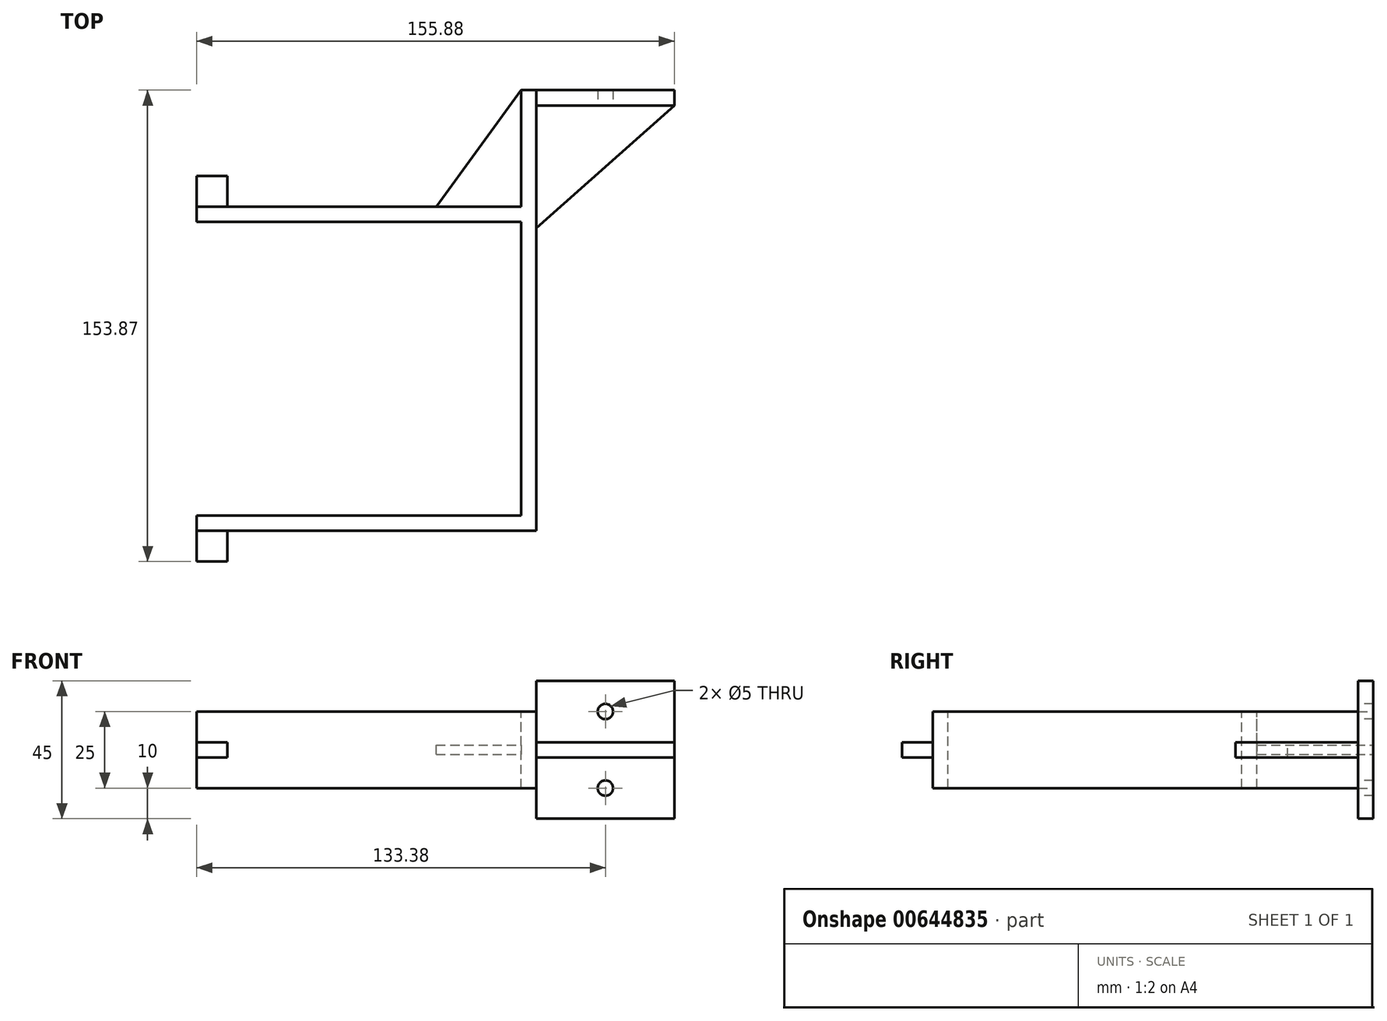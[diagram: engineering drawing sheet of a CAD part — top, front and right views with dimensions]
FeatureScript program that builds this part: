
annotation { "Feature Type Name" : "Feature", "Feature Type Description" : "" }
export const myFeature = defineFeature(function(context is Context, id is Id, definition is map)
    precondition{}
    {
        {
            var Q0;
            Q0=qCreatedBy(makeId("Top.planeOp"),FACE);
            var sketch = newSketch(context, id + "F0", { "sketchPlane" : qUnion([Q0])});
            skLineSegment(sketch, "E0", {"start": v(0, 0) * mm, "end": v(0, 0) * mm});
            skLineSegment(sketch, "E1", {"start": v(0, 0) * mm, "end": v(-10, 0) * mm});
            skLineSegment(sketch, "E2", {"start": v(-10, 0) * mm, "end": v(-10, -5) * mm});
            skLineSegment(sketch, "E3", {"start": v(-10, -5) * mm, "end": v(100.88, -5) * mm});
            skLineSegment(sketch, "E4", {"start": v(100.88, -5) * mm, "end": v(100.88, 133.87) * mm});
            skLineSegment(sketch, "E5", {"start": v(100.88, 133.87) * mm, "end": v(145.88, 133.87) * mm});
            skLineSegment(sketch, "E6", {"start": v(145.88, 133.87) * mm, "end": v(145.88, 138.87) * mm});
            skLineSegment(sketch, "E7", {"start": v(145.88, 138.87) * mm, "end": v(95.88, 138.87) * mm});
            skLineSegment(sketch, "E8", {"start": v(95.88, 138.87) * mm, "end": v(95.88, 100.88) * mm});
            skLineSegment(sketch, "E9", {"start": v(95.88, 100.88) * mm, "end": v(-10, 100.88) * mm});
            skLineSegment(sketch, "E10", {"start": v(-10, 100.88) * mm, "end": v(-10, 95.88) * mm});
            skLineSegment(sketch, "E11", {"start": v(-10, 95.88) * mm, "end": v(0, 95.88) * mm});
            skLineSegment(sketch, "E12", {"start": v(0, 95.88) * mm, "end": v(0, 95.88) * mm});
            skLineSegment(sketch, "E13", {"start": v(0, 95.88) * mm, "end": v(95.88, 95.88) * mm});
            skLineSegment(sketch, "E14", {"start": v(95.88, 95.88) * mm, "end": v(95.88, 0) * mm});
            skLineSegment(sketch, "E15", {"start": v(95.88, 0) * mm, "end": v(0, 0) * mm});
            skSolve(sketch);
        }
        {
            var Q0;
            Q0=qSketchRegion(id+"F0",true);
            extrude(context, id + "F1", {"entities" : qUnion([Q0]), "oppositeDirection" : true, "depth" : 25 * mm, "offsetDistance" : 25 * mm});
        }
        {
            var Q0;
            Q0=makeQuery(id+"F1.opExtrude","SWEPT_FACE",FACE,{"disambiguationData":[OSD([sQuery(id+"F0.wireOp",EDGE,"E7")])]});
            var sketch = newSketch(context, id + "F2", { "sketchPlane" : qUnion([Q0])});
            skLineSegment(sketch, "E16.bottom", {"start": v(-95.88, -17) * mm, "end": v(-56.33, -17) * mm});
            skLineSegment(sketch, "E16.top", {"start": v(-95.88, -8) * mm, "end": v(-56.33, -8) * mm});
            skLineSegment(sketch, "E16.left", {"start": v(-95.88, -17) * mm, "end": v(-95.88, -8) * mm});
            skLineSegment(sketch, "E16.right", {"start": v(-56.33, -17) * mm, "end": v(-56.33, -8) * mm});
            skSolve(sketch);
        }
        {
            var Q0;
            Q0=makeQuery(id+"F2.imprint","IMPRINT",FACE,{"disambiguationData":[TD([[makeQuery(id+"F2.imprint","IMPRINT",EDGE,{"derivedFrom":sQuery(id+"F2.wireOp",EDGE,"E16.bottom")}),1.0]])]});
            extrude(context, id + "F3", {"entities" : qUnion([Q0]), "operationType" : NewBodyOperationType.REMOVE, "oppositeDirection" : true, "depth" : 33 * mm, "offsetDistance" : 25 * mm});
        }
        {
            var Q0;
            Q0=makeQuery(id+"F1.opExtrude","SWEPT_FACE",FACE,{"disambiguationData":[OSD([sQuery(id+"F0.wireOp",EDGE,"E3")])]});
            var sketch = newSketch(context, id + "F4", { "sketchPlane" : qUnion([Q0])});
            skLineSegment(sketch, "E17.bottom", {"start": v(-10, -15) * mm, "end": v(0, -15) * mm});
            skLineSegment(sketch, "E17.top", {"start": v(-10, -10) * mm, "end": v(0, -10) * mm});
            skLineSegment(sketch, "E17.left", {"start": v(-10, -15) * mm, "end": v(-10, -10) * mm});
            skLineSegment(sketch, "E17.right", {"start": v(0, -15) * mm, "end": v(0, -10) * mm});
            skSolve(sketch);
        }
        {
            var Q0;
            Q0=makeQuery(id+"F4.imprint","IMPRINT",FACE,{"disambiguationData":[TD([[makeQuery(id+"F4.imprint","IMPRINT",EDGE,{"derivedFrom":sQuery(id+"F4.wireOp",EDGE,"E17.bottom")}),1.0]])]});
            extrude(context, id + "F5", {"entities" : qUnion([Q0]), "operationType" : NewBodyOperationType.ADD, "depth" : 10 * mm, "offsetDistance" : 25 * mm});
        }
        {
            var Q0;
            Q0=makeQuery(id+"F3.boolean.opBoolean","MERGE",FACE,{"derivedFrom":[makeQuery(id+"F1.opExtrude","SWEPT_FACE",FACE,{"disambiguationData":[OSD([sQuery(id+"F0.wireOp",EDGE,"E9")])]}),makeQuery(id+"F3.opExtrude","CAP_FACE",FACE,{"disambiguationData":[OSD([sQuery(id+"F2.wireOp",EDGE,"E16.bottom"),sQuery(id+"F2.wireOp",EDGE,"E16.top"),sQuery(id+"F2.wireOp",EDGE,"E16.left"),sQuery(id+"F2.wireOp",EDGE,"E16.right")])],"isStart":false})]});
            var sketch = newSketch(context, id + "F6", { "sketchPlane" : qUnion([Q0])});
            skLineSegment(sketch, "E18.bottom", {"start": v(10, -10) * mm, "end": v(0, -10) * mm});
            skLineSegment(sketch, "E18.top", {"start": v(10, -15) * mm, "end": v(0, -15) * mm});
            skLineSegment(sketch, "E18.left", {"start": v(10, -10) * mm, "end": v(10, -15) * mm});
            skLineSegment(sketch, "E18.right", {"start": v(0, -10) * mm, "end": v(0, -15) * mm});
            skSolve(sketch);
        }
        {
            var Q0;
            Q0=makeQuery(id+"F6.imprint","IMPRINT",FACE,{"disambiguationData":[TD([[makeQuery(id+"F6.imprint","IMPRINT",EDGE,{"derivedFrom":sQuery(id+"F6.wireOp",EDGE,"E18.bottom")}),1.0]])]});
            extrude(context, id + "F7", {"entities" : qUnion([Q0]), "operationType" : NewBodyOperationType.ADD, "depth" : 10 * mm, "offsetDistance" : 25 * mm});
        }
        {
            var Q0;
            Q0=makeQuery(id+"F1.opExtrude","SWEPT_FACE",FACE,{"disambiguationData":[OSD([sQuery(id+"F0.wireOp",EDGE,"E5")])]});
            var sketch = newSketch(context, id + "F8", { "sketchPlane" : qUnion([Q0])});
            skLineSegment(sketch, "E19.bottom", {"start": v(100.88, -10) * mm, "end": v(145.88, -10) * mm});
            skLineSegment(sketch, "E19.top", {"start": v(100.88, -15) * mm, "end": v(145.88, -15) * mm});
            skLineSegment(sketch, "E19.left", {"start": v(100.88, -10) * mm, "end": v(100.88, -15) * mm});
            skLineSegment(sketch, "E19.right", {"start": v(145.88, -10) * mm, "end": v(145.88, -15) * mm});
            skSolve(sketch);
        }
        {
            var Q0;
            Q0=makeQuery(id+"F8.imprint","IMPRINT",FACE,{"disambiguationData":[TD([[makeQuery(id+"F8.imprint","IMPRINT",EDGE,{"derivedFrom":sQuery(id+"F8.wireOp",EDGE,"E19.bottom")}),-1.0]])]});
            extrude(context, id + "F9", {"entities" : qUnion([Q0]), "operationType" : NewBodyOperationType.ADD, "depth" : 40 * mm, "offsetDistance" : 25 * mm});
        }
        {
            var Q0;
            Q0=makeQuery(id+"F9.opExtrude","SWEPT_FACE",FACE,{"disambiguationData":[OSD([sQuery(id+"F8.wireOp",EDGE,"E19.top")])]});
            var sketch = newSketch(context, id + "F10", { "sketchPlane" : qUnion([Q0])});
            skLineSegment(sketch, "E20", {"start": v(100.88, -93.87) * mm, "end": v(145.88, -133.87) * mm});
            skLineSegment(sketch, "E21", {"start": v(100.88, -93.87) * mm, "end": v(145.88, -93.87) * mm});
            skLineSegment(sketch, "E22", {"start": v(145.88, -93.87) * mm, "end": v(145.88, -133.87) * mm});
            skLineSegment(sketch, "E23", {"start": v(145.88, -67.74) * mm, "end": v(136.05, -67.74) * mm});
            skSolve(sketch);
        }
        {
            var Q0;
            Q0=makeQuery(id+"F10.imprint","IMPRINT",FACE,{"disambiguationData":[TD([[makeQuery(id+"F10.imprint","IMPRINT",EDGE,{"derivedFrom":sQuery(id+"F10.wireOp",EDGE,"E20")}),1.0]])]});
            extrude(context, id + "F11", {"entities" : qUnion([Q0]), "operationType" : NewBodyOperationType.REMOVE, "endBound" : BoundingType.UP_TO_NEXT, "oppositeDirection" : true, "depth" : 25 * mm, "offsetDistance" : 25 * mm});
        }
        {
            var Q0;
            {var subQ0=sQuery(id+"F0.wireOp",EDGE,"E9");var subQ1=sQuery(id+"F0.wireOp",EDGE,"E8");Q0=makeQuery(id+"F3OWXgqpNNXNJOV_1.boolean.opBoolean","MERGE",FACE,{"derivedFrom":[makeQuery(id+"F1.opExtrude","CAP_FACE",FACE,{"disambiguationData":[OSD([sQuery(id+"F0.wireOp",EDGE,"E1"),sQuery(id+"F0.wireOp",EDGE,"E2"),sQuery(id+"F0.wireOp",EDGE,"E3"),sQuery(id+"F0.wireOp",EDGE,"E4"),sQuery(id+"F0.wireOp",EDGE,"E5"),sQuery(id+"F0.wireOp",EDGE,"E6"),sQuery(id+"F0.wireOp",EDGE,"E7"),subQ1,subQ0,sQuery(id+"F0.wireOp",EDGE,"E10"),sQuery(id+"F0.wireOp",EDGE,"E11"),sQuery(id+"F0.wireOp",EDGE,"E13"),sQuery(id+"F0.wireOp",EDGE,"E14"),sQuery(id+"F0.wireOp",EDGE,"E15")])],"isStart":false}),makeQuery(id+"F3OWXgqpNNXNJOV_1.opExtrude","CAP_FACE",FACE,{"disambiguationData":[OSD([subQ1,subQ0,sQuery(id+"FQ3WUeavLo7wkBa_1.wireOp",EDGE,"9ih6puce-coCi-Da0f-sg7k-QBfH5EJdpGK5")])],"isStart":false})]});}
            var sketch = newSketch(context, id + "F12", { "sketchPlane" : qUnion([Q0])});
            skLineSegment(sketch, "E24.bottom", {"start": v(100.88, -133.87) * mm, "end": v(145.88, -133.87) * mm});
            skLineSegment(sketch, "E24.top", {"start": v(100.88, -138.87) * mm, "end": v(145.88, -138.87) * mm});
            skLineSegment(sketch, "E24.left", {"start": v(100.88, -133.87) * mm, "end": v(100.88, -138.87) * mm});
            skLineSegment(sketch, "E24.right", {"start": v(145.88, -133.87) * mm, "end": v(145.88, -138.87) * mm});
            skSolve(sketch);
        }
        {
            var Q0;
            Q0=makeQuery(id+"F12.imprint","IMPRINT",FACE,{"disambiguationData":[TD([[makeQuery(id+"F12.imprint","IMPRINT",EDGE,{"derivedFrom":sQuery(id+"F12.wireOp",EDGE,"E24.bottom")}),-1.0]])]});
            extrude(context, id + "F13", {"entities" : qUnion([Q0]), "operationType" : NewBodyOperationType.ADD, "depth" : 10 * mm, "offsetDistance" : 25 * mm});
        }
        {
            var Q0;
            {var subQ0=sQuery(id+"F0.wireOp",EDGE,"E9");var subQ1=sQuery(id+"F0.wireOp",EDGE,"E8");Q0=makeQuery(id+"F3OWXgqpNNXNJOV_1.boolean.opBoolean","MERGE",FACE,{"derivedFrom":[makeQuery(id+"F1.opExtrude","CAP_FACE",FACE,{"disambiguationData":[OSD([sQuery(id+"F0.wireOp",EDGE,"E1"),sQuery(id+"F0.wireOp",EDGE,"E2"),sQuery(id+"F0.wireOp",EDGE,"E3"),sQuery(id+"F0.wireOp",EDGE,"E4"),sQuery(id+"F0.wireOp",EDGE,"E5"),sQuery(id+"F0.wireOp",EDGE,"E6"),sQuery(id+"F0.wireOp",EDGE,"E7"),subQ1,subQ0,sQuery(id+"F0.wireOp",EDGE,"E10"),sQuery(id+"F0.wireOp",EDGE,"E11"),sQuery(id+"F0.wireOp",EDGE,"E13"),sQuery(id+"F0.wireOp",EDGE,"E14"),sQuery(id+"F0.wireOp",EDGE,"E15")])],"isStart":true}),makeQuery(id+"F3OWXgqpNNXNJOV_1.opExtrude","CAP_FACE",FACE,{"disambiguationData":[OSD([subQ1,subQ0,sQuery(id+"FQ3WUeavLo7wkBa_1.wireOp",EDGE,"9ih6puce-coCi-Da0f-sg7k-QBfH5EJdpGK5")])],"isStart":true})]});}
            var sketch = newSketch(context, id + "F14", { "sketchPlane" : qUnion([Q0])});
            skLineSegment(sketch, "E25.bottom", {"start": v(100.88, 133.87) * mm, "end": v(145.88, 133.87) * mm});
            skLineSegment(sketch, "E25.top", {"start": v(100.88, 138.87) * mm, "end": v(145.88, 138.87) * mm});
            skLineSegment(sketch, "E25.left", {"start": v(100.88, 133.87) * mm, "end": v(100.88, 138.87) * mm});
            skLineSegment(sketch, "E25.right", {"start": v(145.88, 133.87) * mm, "end": v(145.88, 138.87) * mm});
            skSolve(sketch);
        }
        {
            var Q0;
            Q0=makeQuery(id+"F14.imprint","IMPRINT",FACE,{"disambiguationData":[TD([[makeQuery(id+"F14.imprint","IMPRINT",EDGE,{"derivedFrom":sQuery(id+"F14.wireOp",EDGE,"E25.bottom")}),1.0]])]});
            extrude(context, id + "F15", {"entities" : qUnion([Q0]), "operationType" : NewBodyOperationType.ADD, "depth" : 10 * mm, "offsetDistance" : 25 * mm});
        }
        {
            var Q0;
            Q0=makeQuery(id+"F1.opExtrude","SWEPT_FACE",FACE,{"disambiguationData":[OSD([sQuery(id+"F0.wireOp",EDGE,"E8")])]});
            var sketch = newSketch(context, id + "F16", { "sketchPlane" : qUnion([Q0])});
            skLineSegment(sketch, "E26.bottom", {"start": v(-100.88, -11) * mm, "end": v(-138.87, -11) * mm});
            skLineSegment(sketch, "E26.top", {"start": v(-100.88, -14) * mm, "end": v(-138.87, -14) * mm});
            skLineSegment(sketch, "E26.left", {"start": v(-100.88, -11) * mm, "end": v(-100.88, -14) * mm});
            skLineSegment(sketch, "E26.right", {"start": v(-138.87, -11) * mm, "end": v(-138.87, -14) * mm});
            skSolve(sketch);
        }
        {
            var Q0;
            Q0=makeQuery(id+"F16.imprint","IMPRINT",FACE,{"disambiguationData":[TD([[makeQuery(id+"F16.imprint","IMPRINT",EDGE,{"derivedFrom":sQuery(id+"F16.wireOp",EDGE,"E26.bottom")}),1.0]])]});
            extrude(context, id + "F17", {"entities" : qUnion([Q0]), "operationType" : NewBodyOperationType.ADD, "depth" : 27.7 * mm, "offsetDistance" : 25 * mm});
        }
        {
            var Q0;
            Q0=makeQuery(id+"F17.opExtrude","SWEPT_FACE",FACE,{"disambiguationData":[OSD([sQuery(id+"F16.wireOp",EDGE,"E26.top")])]});
            var sketch = newSketch(context, id + "F18", { "sketchPlane" : qUnion([Q0])});
            skLineSegment(sketch, "E27", {"start": v(95.88, -138.87) * mm, "end": v(68.18, -100.88) * mm});
            skLineSegment(sketch, "E28", {"start": v(68.18, -100.88) * mm, "end": v(68.18, -138.87) * mm});
            skLineSegment(sketch, "E29", {"start": v(68.18, -138.87) * mm, "end": v(95.88, -138.87) * mm});
            skSolve(sketch);
        }
        {
            var Q0;
            Q0=makeQuery(id+"F18.imprint","IMPRINT",FACE,{"disambiguationData":[TD([[makeQuery(id+"F18.imprint","IMPRINT",EDGE,{"derivedFrom":sQuery(id+"F18.wireOp",EDGE,"E27")}),1.0]])]});
            extrude(context, id + "F19", {"entities" : qUnion([Q0]), "operationType" : NewBodyOperationType.REMOVE, "oppositeDirection" : true, "depth" : 25 * mm, "offsetDistance" : 25 * mm});
        }
        {
            var Q0;
            {var subQ2=sQuery(id+"F0.wireOp",EDGE,"E5");Q0=makeQuery(id+"F15.boolean.opBoolean","MERGE",FACE,{"derivedFrom":[makeQuery(id+"F9.boolean.opBoolean","SPLIT",FACE,{"disambiguationData":[TD([makeQuery(id+"F9.opExtrude","SWEPT_FACE",FACE,{"disambiguationData":[OSD([sQuery(id+"F8.wireOp",EDGE,"E19.bottom")])]})])],"derivedFrom":makeQuery(id+"F1.opExtrude","SWEPT_FACE",FACE,{"disambiguationData":[OSD([subQ2])]})}),makeQuery(id+"F15.opExtrude","SWEPT_FACE",FACE,{"disambiguationData":[OSD([sQuery(id+"F14.wireOp",EDGE,"E25.bottom")])]})]});}
            var sketch = newSketch(context, id + "F20", { "sketchPlane" : qUnion([Q0])});
            skCircle(sketch, "E30", {"center": v(123.38, 0) * mm, "radius": 2.5 * mm});
            skCircle(sketch, "E31", {"center": v(123.38, -25) * mm, "radius": 2.5 * mm});
            skSolve(sketch);
        }
        {
            var Q0;
            Q0=makeQuery(id+"F20.imprint","IMPRINT",FACE,{"disambiguationData":[TD([[makeQuery(id+"F20.imprint","IMPRINT",EDGE,{"derivedFrom":sQuery(id+"F20.wireOp",EDGE,"E30")}),1.0]])]});
            var Q1;
            Q1=makeQuery(id+"F20.imprint","IMPRINT",FACE,{"disambiguationData":[TD([[makeQuery(id+"F20.imprint","IMPRINT",EDGE,{"derivedFrom":sQuery(id+"F20.wireOp",EDGE,"E31")}),1.0]])]});
            extrude(context, id + "F21", {"entities" : qUnion([Q0, Q1]), "operationType" : NewBodyOperationType.REMOVE, "endBound" : BoundingType.UP_TO_NEXT, "oppositeDirection" : true, "depth" : 25 * mm, "offsetDistance" : 25 * mm});
        }
    });
